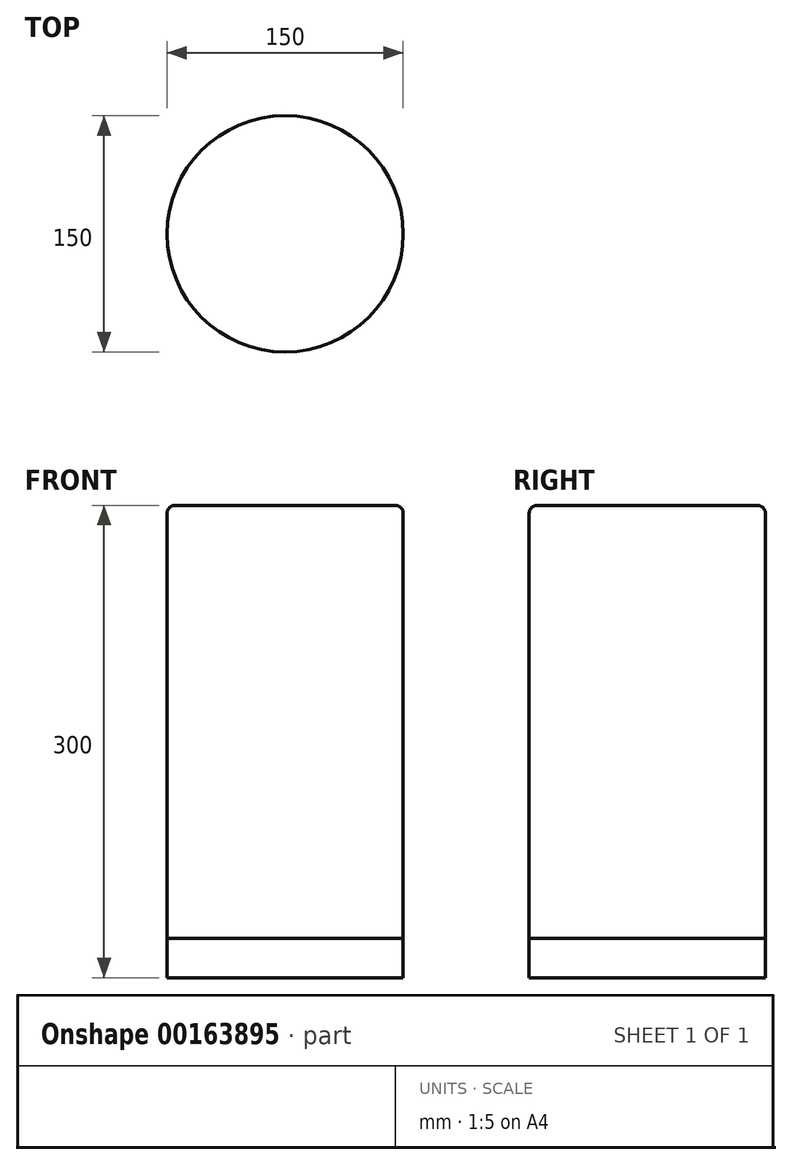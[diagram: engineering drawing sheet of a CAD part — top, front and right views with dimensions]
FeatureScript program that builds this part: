
annotation { "Feature Type Name" : "Feature", "Feature Type Description" : "" }
export const myFeature = defineFeature(function(context is Context, id is Id, definition is map)
    precondition{}
    {
        {
            var Q0;
            Q0=qCreatedBy(makeId("Top.planeOp"),FACE);
            var sketch = newSketch(context, id + "F0", { "sketchPlane" : qUnion([Q0])});
            skCircle(sketch, "E0", {"center": v(0, 0) * mm, "radius": 75 * mm});
            skSolve(sketch);
        }
        {
            var Q0;
            Q0=makeQuery(id+"F0.imprint","IMPRINT",FACE,{"disambiguationData":[TD([[makeQuery(id+"F0.imprint","IMPRINT",EDGE,{"derivedFrom":sQuery(id+"F0.wireOp",EDGE,"E0")}),1.0]])]});
            extrude(context, id + "F1", {"entities" : qUnion([Q0]), "depth" : 300 * mm});
        }
        {
            var Q0;
            Q0=makeQuery(id+"F1.opExtrude","CAP_EDGE",EDGE,{"disambiguationData":[OSD([sQuery(id+"F0.wireOp",EDGE,"E0")])],"isStart":false});
            var Q1;
            Q1=makeQuery(id+"F1.opExtrude","CAP_FACE",FACE,{"disambiguationData":[OSD([sQuery(id+"F0.wireOp",EDGE,"E0")])],"isStart":false});
            fillet(context, id + "F2", {"entities" : qUnion([Q0, Q1]), "radius" : 5 * mm, "tangentPropagation" : true, "allowEdgeOverflow" : false});
        }
        {
            var Q0;
            Q0 = qSketchRegion(id + "F0", true);
            var Q1;
            Q1=makeQuery(id+"F0.imprint","IMPRINT",FACE,{"disambiguationData":[TD([[makeQuery(id+"F0.imprint","IMPRINT",EDGE,{"derivedFrom":sQuery(id+"F0.wireOp",EDGE,"E0")}),1.0]])]});
            extrude(context, id + "F3", {"entities" : qUnion([Q0, Q1]), "depth" : 25 * mm});
        }
    });
